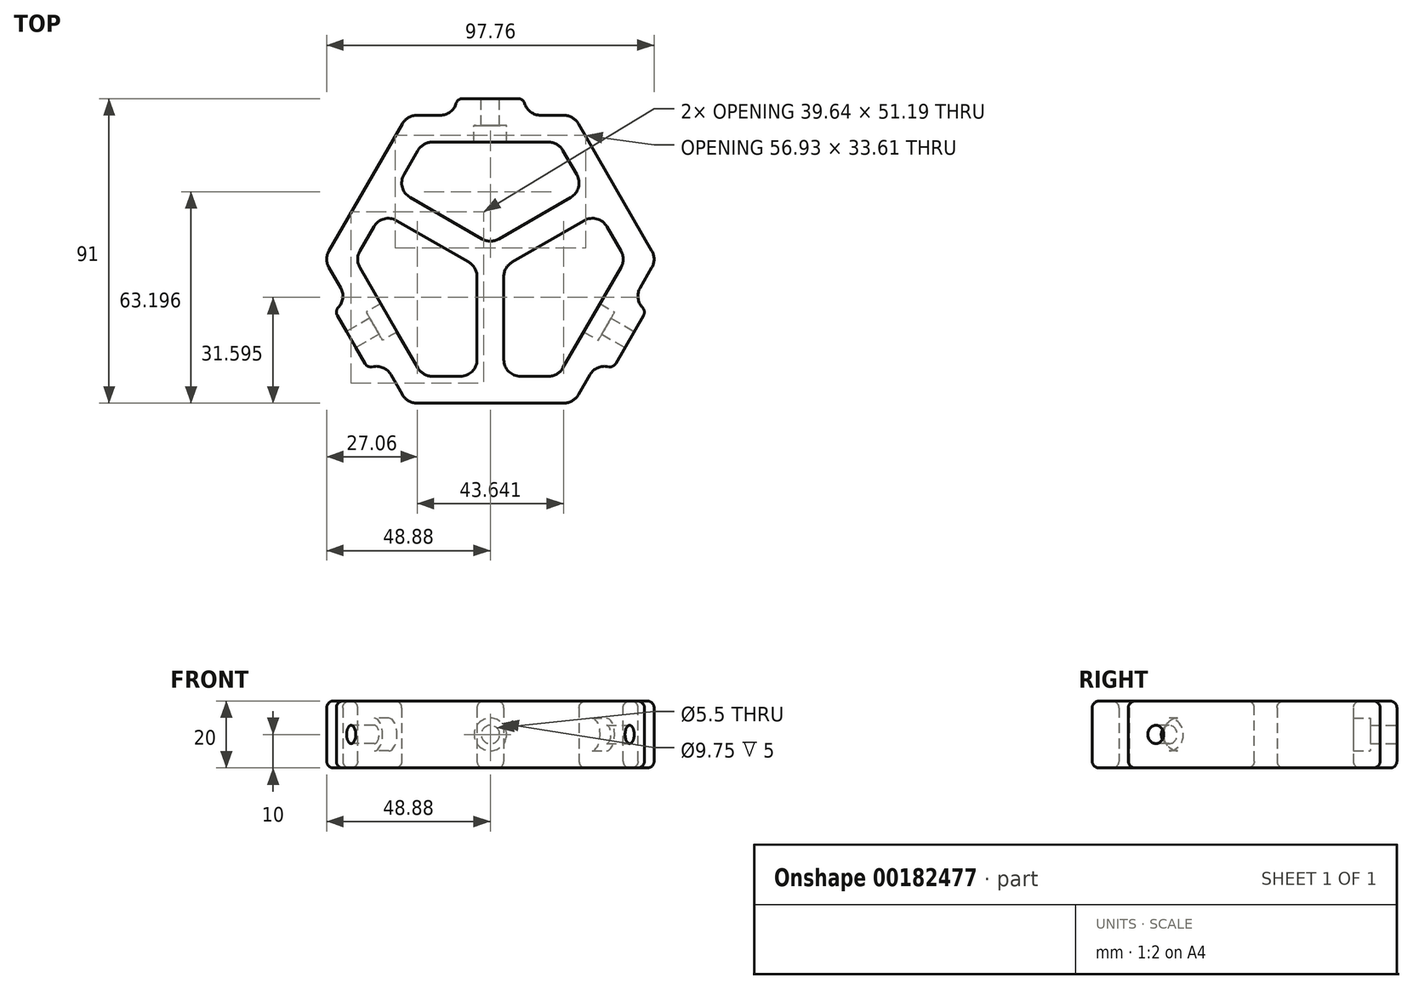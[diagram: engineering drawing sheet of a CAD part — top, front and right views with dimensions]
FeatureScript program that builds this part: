
annotation { "Feature Type Name" : "Feature", "Feature Type Description" : "" }
export const myFeature = defineFeature(function(context is Context, id is Id, definition is map)
    precondition{}
    {
        {
            var Q0;
            Q0=qCreatedBy(makeId("Top.planeOp"),FACE);
            var sketch = newSketch(context, id + "F0", { "sketchPlane" : qUnion([Q0])});
            skCircle(sketch, "E0.cCircle", {"center": v(0, 0) * mm, "radius": 35 * mm, "construction": true});
            skLineSegment(sketch, "E0.0", {"start": v(-20.2, 35) * mm, "end": v(20.2, 35) * mm});
            skLineSegment(sketch, "E0.1", {"start": v(20.2, 35) * mm, "end": v(40.41, 0) * mm});
            skLineSegment(sketch, "E0.2", {"start": v(40.41, 0) * mm, "end": v(20.2, -35) * mm});
            skLineSegment(sketch, "E0.3", {"start": v(20.2, -35) * mm, "end": v(-20.2, -35) * mm});
            skLineSegment(sketch, "E0.4", {"start": v(-20.2, -35) * mm, "end": v(-40.41, 0) * mm});
            skLineSegment(sketch, "E0.5", {"start": v(-40.41, 0) * mm, "end": v(-20.2, 35) * mm});
            skPoint(sketch, "E0.0.midPoint", {"position": v(0, 35) * mm});
            skCircle(sketch, "E1.cCircle", {"center": v(0, 0) * mm, "radius": 43 * mm, "construction": true});
            skLineSegment(sketch, "E1.0", {"start": v(-24.83, 43) * mm, "end": v(24.83, 43) * mm});
            skLineSegment(sketch, "E1.1", {"start": v(24.83, 43) * mm, "end": v(49.65, 0) * mm});
            skLineSegment(sketch, "E1.2", {"start": v(49.65, 0) * mm, "end": v(24.83, -43) * mm});
            skLineSegment(sketch, "E1.3", {"start": v(24.83, -43) * mm, "end": v(-24.83, -43) * mm});
            skLineSegment(sketch, "E1.4", {"start": v(-24.83, -43) * mm, "end": v(-49.65, 0) * mm});
            skLineSegment(sketch, "E1.5", {"start": v(-49.65, 0) * mm, "end": v(-24.83, 43) * mm});
            skPoint(sketch, "E1.0.midPoint", {"position": v(0, 43) * mm});
            skLineSegment(sketch, "E2", {"start": v(0, 0) * mm, "end": v(-37.24, 21.5) * mm, "construction": true});
            skLineSegment(sketch, "E3", {"start": v(0, 0) * mm, "end": v(37.24, 21.5) * mm, "construction": true});
            skLineSegment(sketch, "E4", {"start": v(0, 0) * mm, "end": v(0, -43) * mm, "construction": true});
            skLineSegment(sketch, "E5", {"start": v(-28.31, 20.96) * mm, "end": v(0, 4.62) * mm});
            skLineSegment(sketch, "E6", {"start": v(0, 4.62) * mm, "end": v(28.31, 20.96) * mm});
            skLineSegment(sketch, "E7", {"start": v(32.31, 14.04) * mm, "end": v(4, -2.3) * mm});
            skLineSegment(sketch, "E8", {"start": v(4, -2.3) * mm, "end": v(4, -35) * mm});
            skLineSegment(sketch, "E9", {"start": v(-4, -35) * mm, "end": v(-4, -2.3) * mm});
            skLineSegment(sketch, "E10", {"start": v(-4, -2.3) * mm, "end": v(-32.31, 14.04) * mm});
            skLineSegment(sketch, "E11", {"start": v(-10, 43) * mm, "end": v(-10, 48) * mm});
            skLineSegment(sketch, "E12", {"start": v(-10, 48) * mm, "end": v(10, 48) * mm});
            skLineSegment(sketch, "E13", {"start": v(10, 48) * mm, "end": v(10, 43) * mm});
            skLineSegment(sketch, "E14", {"start": v(42.24, -12.84) * mm, "end": v(46.57, -15.34) * mm});
            skLineSegment(sketch, "E15", {"start": v(46.57, -15.34) * mm, "end": v(36.57, -32.66) * mm});
            skLineSegment(sketch, "E16", {"start": v(36.57, -32.66) * mm, "end": v(32.24, -30.16) * mm});
            skLineSegment(sketch, "E17", {"start": v(-42.24, -12.84) * mm, "end": v(-46.57, -15.34) * mm});
            skLineSegment(sketch, "E18", {"start": v(-46.57, -15.34) * mm, "end": v(-36.57, -32.66) * mm});
            skPoint(sketch, "E19", {"position": v(-37.24, -21.5) * mm});
            skPoint(sketch, "E20", {"position": v(37.24, -21.5) * mm});
            skLineSegment(sketch, "E21", {"start": v(-36.57, -32.66) * mm, "end": v(-32.24, -30.16) * mm});
            skSolve(sketch);
        }
        {
            var Q0;
            Q0=makeQuery(id+"F0.imprint","IMPRINT",FACE,{"disambiguationData":[TD([[makeQuery(id+"F0.imprint","IMPRINT",EDGE,{"derivedFrom":sQuery(id+"F0.wireOp",EDGE,"E0.0")}),1.0]])]});
            var Q1;
            {var subQ0=sQuery(id+"F0.wireOp",EDGE,"E5");Q1=makeQuery(id+"F0.imprint","IMPRINT",FACE,{"disambiguationData":[TD([[makeQuery(id+"F0.imprint","IMPRINT",EDGE,{"derivedFrom":subQ0}),-1.0]])]});}
            var Q2;
            {var subQ2=sQuery(id+"F0.wireOp",EDGE,"E17");Q2=makeQuery(id+"F0.imprint","IMPRINT",FACE,{"disambiguationData":[TD([[makeQuery(id+"F0.imprint","IMPRINT",EDGE,{"derivedFrom":subQ2}),1.0]])]});}
            var Q3;
            {var subQ0=sQuery(id+"F0.wireOp",EDGE,"E14");Q3=makeQuery(id+"F0.imprint","IMPRINT",FACE,{"disambiguationData":[TD([[makeQuery(id+"F0.imprint","IMPRINT",EDGE,{"derivedFrom":subQ0}),-1.0]])]});}
            var Q4;
            {var subQ0=sQuery(id+"F0.wireOp",EDGE,"E11");Q4=makeQuery(id+"F0.imprint","IMPRINT",FACE,{"disambiguationData":[TD([[makeQuery(id+"F0.imprint","IMPRINT",EDGE,{"derivedFrom":subQ0}),-1.0]])]});}
            extrude(context, id + "F1", {"entities" : qUnion([Q0, Q1, Q2, Q3, Q4]), "depth" : 20 * mm, "offsetDistance" : 25 * mm});
        }
        {
            var Q0;
            Q0=makeQuery(id+"F1.opExtrude","SWEPT_EDGE",EDGE,{"disambiguationData":[OSD([sQuery(id+"F0.wireOp",EDGE,"E1.4"),sQuery(id+"F0.wireOp",EDGE,"E1.5")])]});
            var Q1;
            Q1=makeQuery(id+"F1.opExtrude","SWEPT_EDGE",EDGE,{"disambiguationData":[OSD([sQuery(id+"F0.wireOp",EDGE,"E1.0"),sQuery(id+"F0.wireOp",EDGE,"E1.5")])]});
            var Q2;
            Q2=makeQuery(id+"F1.opExtrude","SWEPT_EDGE",EDGE,{"disambiguationData":[OSD([sQuery(id+"F0.wireOp",EDGE,"E1.0"),sQuery(id+"F0.wireOp",EDGE,"E1.1")])]});
            var Q3;
            Q3=makeQuery(id+"F1.opExtrude","SWEPT_EDGE",EDGE,{"disambiguationData":[OSD([sQuery(id+"F0.wireOp",EDGE,"E1.1"),sQuery(id+"F0.wireOp",EDGE,"E1.2")])]});
            var Q4;
            Q4=makeQuery(id+"F1.opExtrude","SWEPT_EDGE",EDGE,{"disambiguationData":[OSD([sQuery(id+"F0.wireOp",EDGE,"E1.2"),sQuery(id+"F0.wireOp",EDGE,"E1.3")])]});
            var Q5;
            Q5=makeQuery(id+"F1.opExtrude","SWEPT_EDGE",EDGE,{"disambiguationData":[OSD([sQuery(id+"F0.wireOp",EDGE,"E1.3"),sQuery(id+"F0.wireOp",EDGE,"E1.4")])]});
            var Q6;
            Q6=makeQuery(id+"F1.opExtrude","SWEPT_EDGE",EDGE,{"disambiguationData":[OSD([sQuery(id+"F0.wireOp",EDGE,"E0.4"),sQuery(id+"F0.wireOp",EDGE,"E0.5")])]});
            var Q7;
            Q7=makeQuery(id+"F1.opExtrude","SWEPT_EDGE",EDGE,{"disambiguationData":[OSD([sQuery(id+"F0.wireOp",EDGE,"E0.5"),sQuery(id+"F0.wireOp",EDGE,"E10")])]});
            var Q8;
            Q8=makeQuery(id+"F1.opExtrude","SWEPT_EDGE",EDGE,{"disambiguationData":[OSD([sQuery(id+"F0.wireOp",EDGE,"E0.5"),sQuery(id+"F0.wireOp",EDGE,"E5")])]});
            var Q9;
            Q9=makeQuery(id+"F1.opExtrude","SWEPT_EDGE",EDGE,{"disambiguationData":[OSD([sQuery(id+"F0.wireOp",EDGE,"E0.0"),sQuery(id+"F0.wireOp",EDGE,"E0.5")])]});
            var Q10;
            Q10=makeQuery(id+"F1.opExtrude","SWEPT_EDGE",EDGE,{"disambiguationData":[OSD([sQuery(id+"F0.wireOp",EDGE,"E0.0"),sQuery(id+"F0.wireOp",EDGE,"E0.1")])]});
            var Q11;
            Q11=makeQuery(id+"F1.opExtrude","SWEPT_EDGE",EDGE,{"disambiguationData":[OSD([sQuery(id+"F0.wireOp",EDGE,"E0.1"),sQuery(id+"F0.wireOp",EDGE,"E6")])]});
            var Q12;
            Q12=makeQuery(id+"F1.opExtrude","SWEPT_EDGE",EDGE,{"disambiguationData":[OSD([sQuery(id+"F0.wireOp",EDGE,"E5"),sQuery(id+"F0.wireOp",EDGE,"E6")])]});
            var Q13;
            Q13=makeQuery(id+"F1.opExtrude","SWEPT_EDGE",EDGE,{"disambiguationData":[OSD([sQuery(id+"F0.wireOp",EDGE,"E7"),sQuery(id+"F0.wireOp",EDGE,"E8")])]});
            var Q14;
            Q14=makeQuery(id+"F1.opExtrude","SWEPT_EDGE",EDGE,{"disambiguationData":[OSD([sQuery(id+"F0.wireOp",EDGE,"E0.1"),sQuery(id+"F0.wireOp",EDGE,"E7")])]});
            var Q15;
            Q15=makeQuery(id+"F1.opExtrude","SWEPT_EDGE",EDGE,{"disambiguationData":[OSD([sQuery(id+"F0.wireOp",EDGE,"E0.1"),sQuery(id+"F0.wireOp",EDGE,"E0.2")])]});
            var Q16;
            Q16=makeQuery(id+"F1.opExtrude","SWEPT_EDGE",EDGE,{"disambiguationData":[OSD([sQuery(id+"F0.wireOp",EDGE,"E0.3"),sQuery(id+"F0.wireOp",EDGE,"E8")])]});
            var Q17;
            Q17=makeQuery(id+"F1.opExtrude","SWEPT_EDGE",EDGE,{"disambiguationData":[OSD([sQuery(id+"F0.wireOp",EDGE,"E0.2"),sQuery(id+"F0.wireOp",EDGE,"E0.3")])]});
            var Q18;
            Q18=makeQuery(id+"F1.opExtrude","SWEPT_EDGE",EDGE,{"disambiguationData":[OSD([sQuery(id+"F0.wireOp",EDGE,"E9"),sQuery(id+"F0.wireOp",EDGE,"E10")])]});
            var Q19;
            Q19=makeQuery(id+"F1.opExtrude","SWEPT_EDGE",EDGE,{"disambiguationData":[OSD([sQuery(id+"F0.wireOp",EDGE,"E0.3"),sQuery(id+"F0.wireOp",EDGE,"E9")])]});
            var Q20;
            Q20=makeQuery(id+"F1.opExtrude","SWEPT_EDGE",EDGE,{"disambiguationData":[OSD([sQuery(id+"F0.wireOp",EDGE,"E0.3"),sQuery(id+"F0.wireOp",EDGE,"E0.4")])]});
            var Q21;
            Q21=makeQuery(id+"F1.opExtrude","SWEPT_EDGE",EDGE,{"disambiguationData":[OSD([sQuery(id+"F0.wireOp",EDGE,"E1.0"),sQuery(id+"F0.wireOp",EDGE,"E11")])]});
            var Q22;
            Q22=makeQuery(id+"F1.opExtrude","SWEPT_EDGE",EDGE,{"disambiguationData":[OSD([sQuery(id+"F0.wireOp",EDGE,"E1.0"),sQuery(id+"F0.wireOp",EDGE,"E13")])]});
            var Q23;
            Q23=makeQuery(id+"F1.opExtrude","SWEPT_EDGE",EDGE,{"disambiguationData":[OSD([sQuery(id+"F0.wireOp",EDGE,"E1.2"),sQuery(id+"F0.wireOp",EDGE,"E14")])]});
            var Q24;
            Q24=makeQuery(id+"F1.opExtrude","SWEPT_EDGE",EDGE,{"disambiguationData":[OSD([sQuery(id+"F0.wireOp",EDGE,"E1.2"),sQuery(id+"F0.wireOp",EDGE,"E16")])]});
            var Q25;
            Q25=makeQuery(id+"F1.opExtrude","SWEPT_EDGE",EDGE,{"disambiguationData":[OSD([sQuery(id+"F0.wireOp",EDGE,"E1.4"),sQuery(id+"F0.wireOp",EDGE,"E21")])]});
            var Q26;
            Q26=makeQuery(id+"F1.opExtrude","SWEPT_EDGE",EDGE,{"disambiguationData":[OSD([sQuery(id+"F0.wireOp",EDGE,"E1.4"),sQuery(id+"F0.wireOp",EDGE,"E17")])]});
            fillet(context, id + "F2", {"entities" : qUnion([Q0, Q1, Q2, Q3, Q4, Q5, Q6, Q7, Q8, Q9, Q10, Q11, Q12, Q13, Q14, Q15, Q16, Q17, Q18, Q19, Q20, Q21, Q22, Q23, Q24, Q25, Q26]), "tangentPropagation" : true, "radius" : 5 * mm, "defaultsChanged" : false, "vertexSettings" : [], "allowEdgeOverflow" : false});
        }
        {
            var Q0;
            Q0=makeQuery(id+"F1.opExtrude","CAP_FACE",FACE,{"disambiguationData":[OSD([sQuery(id+"F0.wireOp",EDGE,"E0.0"),sQuery(id+"F0.wireOp",EDGE,"E0.1"),sQuery(id+"F0.wireOp",EDGE,"E0.2"),sQuery(id+"F0.wireOp",EDGE,"E0.3"),sQuery(id+"F0.wireOp",EDGE,"E0.4"),sQuery(id+"F0.wireOp",EDGE,"E0.5"),sQuery(id+"F0.wireOp",EDGE,"E1.0"),sQuery(id+"F0.wireOp",EDGE,"E1.1"),sQuery(id+"F0.wireOp",EDGE,"E1.2"),sQuery(id+"F0.wireOp",EDGE,"E1.3"),sQuery(id+"F0.wireOp",EDGE,"E1.4"),sQuery(id+"F0.wireOp",EDGE,"E1.5"),sQuery(id+"F0.wireOp",EDGE,"E5"),sQuery(id+"F0.wireOp",EDGE,"E6"),sQuery(id+"F0.wireOp",EDGE,"E7"),sQuery(id+"F0.wireOp",EDGE,"E8"),sQuery(id+"F0.wireOp",EDGE,"E9"),sQuery(id+"F0.wireOp",EDGE,"E10")])],"isStart":false});
            var Q1;
            Q1=makeQuery(id+"F1.opExtrude","CAP_FACE",FACE,{"disambiguationData":[OSD([sQuery(id+"F0.wireOp",EDGE,"E0.0"),sQuery(id+"F0.wireOp",EDGE,"E0.1"),sQuery(id+"F0.wireOp",EDGE,"E0.2"),sQuery(id+"F0.wireOp",EDGE,"E0.3"),sQuery(id+"F0.wireOp",EDGE,"E0.4"),sQuery(id+"F0.wireOp",EDGE,"E0.5"),sQuery(id+"F0.wireOp",EDGE,"E1.0"),sQuery(id+"F0.wireOp",EDGE,"E1.1"),sQuery(id+"F0.wireOp",EDGE,"E1.2"),sQuery(id+"F0.wireOp",EDGE,"E1.3"),sQuery(id+"F0.wireOp",EDGE,"E1.4"),sQuery(id+"F0.wireOp",EDGE,"E1.5"),sQuery(id+"F0.wireOp",EDGE,"E5"),sQuery(id+"F0.wireOp",EDGE,"E6"),sQuery(id+"F0.wireOp",EDGE,"E7"),sQuery(id+"F0.wireOp",EDGE,"E8"),sQuery(id+"F0.wireOp",EDGE,"E9"),sQuery(id+"F0.wireOp",EDGE,"E10")])],"isStart":true});
            var Q2;
            Q2=makeQuery(id+"F1.opExtrude","SWEPT_FACE",FACE,{"disambiguationData":[OSD([sQuery(id+"F0.wireOp",EDGE,"E12")])]});
            var Q3;
            Q3=makeQuery(id+"F1.opExtrude","SWEPT_FACE",FACE,{"disambiguationData":[OSD([sQuery(id+"F0.wireOp",EDGE,"E15")])]});
            var Q4;
            Q4=makeQuery(id+"F1.opExtrude","SWEPT_FACE",FACE,{"disambiguationData":[OSD([sQuery(id+"F0.wireOp",EDGE,"E18")])]});
            fillet(context, id + "F3", {"entities" : qUnion([Q0, Q1, Q2, Q3, Q4]), "tangentPropagation" : true, "radius" : 2 * mm, "defaultsChanged" : false, "vertexSettings" : [], "allowEdgeOverflow" : false});
        }
        {
            var Q0;
            Q0=makeQuery(id+"F1.opExtrude","SWEPT_FACE",FACE,{"disambiguationData":[OSD([sQuery(id+"F0.wireOp",EDGE,"E0.2")])]});
            var sketch = newSketch(context, id + "F4", { "sketchPlane" : qUnion([Q0])});
            skLineSegment(sketch, "E22", {"start": v(-17.32, 10) * mm, "end": v(17.32, 10) * mm, "construction": true});
            skPoint(sketch, "E23", {"position": v(0, 10) * mm});
            skSolve(sketch);
        }
        {
            var Q0;
            Q0=makeQuery(id+"F1.opExtrude","SWEPT_FACE",FACE,{"disambiguationData":[OSD([sQuery(id+"F0.wireOp",EDGE,"E0.4")])]});
            var sketch = newSketch(context, id + "F5", { "sketchPlane" : qUnion([Q0])});
            skLineSegment(sketch, "E24", {"start": v(-17.32, 10) * mm, "end": v(17.32, 10) * mm, "construction": true});
            skPoint(sketch, "E25", {"position": v(0, 10) * mm});
            skSolve(sketch);
        }
        {
            var Q0;
            Q0=makeQuery(id+"F1.opExtrude","SWEPT_FACE",FACE,{"disambiguationData":[OSD([sQuery(id+"F0.wireOp",EDGE,"E0.0")])]});
            var sketch = newSketch(context, id + "F6", { "sketchPlane" : qUnion([Q0])});
            skLineSegment(sketch, "E26", {"start": v(-17.32, 10) * mm, "end": v(17.32, 10) * mm, "construction": true});
            skPoint(sketch, "E27", {"position": v(0, 10) * mm});
            skSolve(sketch);
        }
        {
            var Q0;
            Q0=sQuery(id+"F6.wireOp",VERTEX,"E27");
            var Q1;
            Q1=sQuery(id+"F5.wireOp",VERTEX,"E25");
            var Q2;
            Q2=sQuery(id+"F4.wireOp",VERTEX,"E23");
            var Q3;
            Q3=makeQuery(id+"F1.opExtrude","SWEPT_BODY",BODY,{"disambiguationData":[OSD([sQuery(id+"F0.wireOp",EDGE,"E0.0"),sQuery(id+"F0.wireOp",EDGE,"E0.1"),sQuery(id+"F0.wireOp",EDGE,"E0.2"),sQuery(id+"F0.wireOp",EDGE,"E0.3"),sQuery(id+"F0.wireOp",EDGE,"E0.4"),sQuery(id+"F0.wireOp",EDGE,"E0.5"),sQuery(id+"F0.wireOp",EDGE,"E1.0"),sQuery(id+"F0.wireOp",EDGE,"E1.1"),sQuery(id+"F0.wireOp",EDGE,"E1.2"),sQuery(id+"F0.wireOp",EDGE,"E1.3"),sQuery(id+"F0.wireOp",EDGE,"E1.4"),sQuery(id+"F0.wireOp",EDGE,"E1.5"),sQuery(id+"F0.wireOp",EDGE,"E5"),sQuery(id+"F0.wireOp",EDGE,"E6"),sQuery(id+"F0.wireOp",EDGE,"E7"),sQuery(id+"F0.wireOp",EDGE,"E8"),sQuery(id+"F0.wireOp",EDGE,"E9"),sQuery(id+"F0.wireOp",EDGE,"E10"),sQuery(id+"F0.wireOp",EDGE,"E11"),sQuery(id+"F0.wireOp",EDGE,"E12"),sQuery(id+"F0.wireOp",EDGE,"E13"),sQuery(id+"F0.wireOp",EDGE,"E14"),sQuery(id+"F0.wireOp",EDGE,"E15"),sQuery(id+"F0.wireOp",EDGE,"E16"),sQuery(id+"F0.wireOp",EDGE,"E17"),sQuery(id+"F0.wireOp",EDGE,"E18"),sQuery(id+"F0.wireOp",EDGE,"E21")])]});
            hole(context, id + "F7", {"style" : HoleStyle.C_BORE, "endStyle" : HoleEndStyle.BLIND, "standardTappedOrClearance" : lookupTablePath({ "fit" : "Normal", "standard" : "ISO", "size" : "M5", "type" : "Clearance" }), "standardBlindInLast" : lookupTablePath({ "fit" : "Normal", "standard" : "ISO", "engagement" : "75%", "pitch" : "0.8 mm", "size" : "M5", "type" : "Clearance & tapped" }), "holeDiameter" : 5.5 * mm, "cBoreDiameter" : 9.75 * mm, "cBoreDepth" : 5 * mm, "majorDiameter" : 5 * mm, "holeDepth" : 20 * mm, "tappedDepth" : 12 * mm, "tapClearance" : 3, "locations" : qUnion([Q0, Q1, Q2]), "scope" : qUnion([Q3])});
        }
    });
